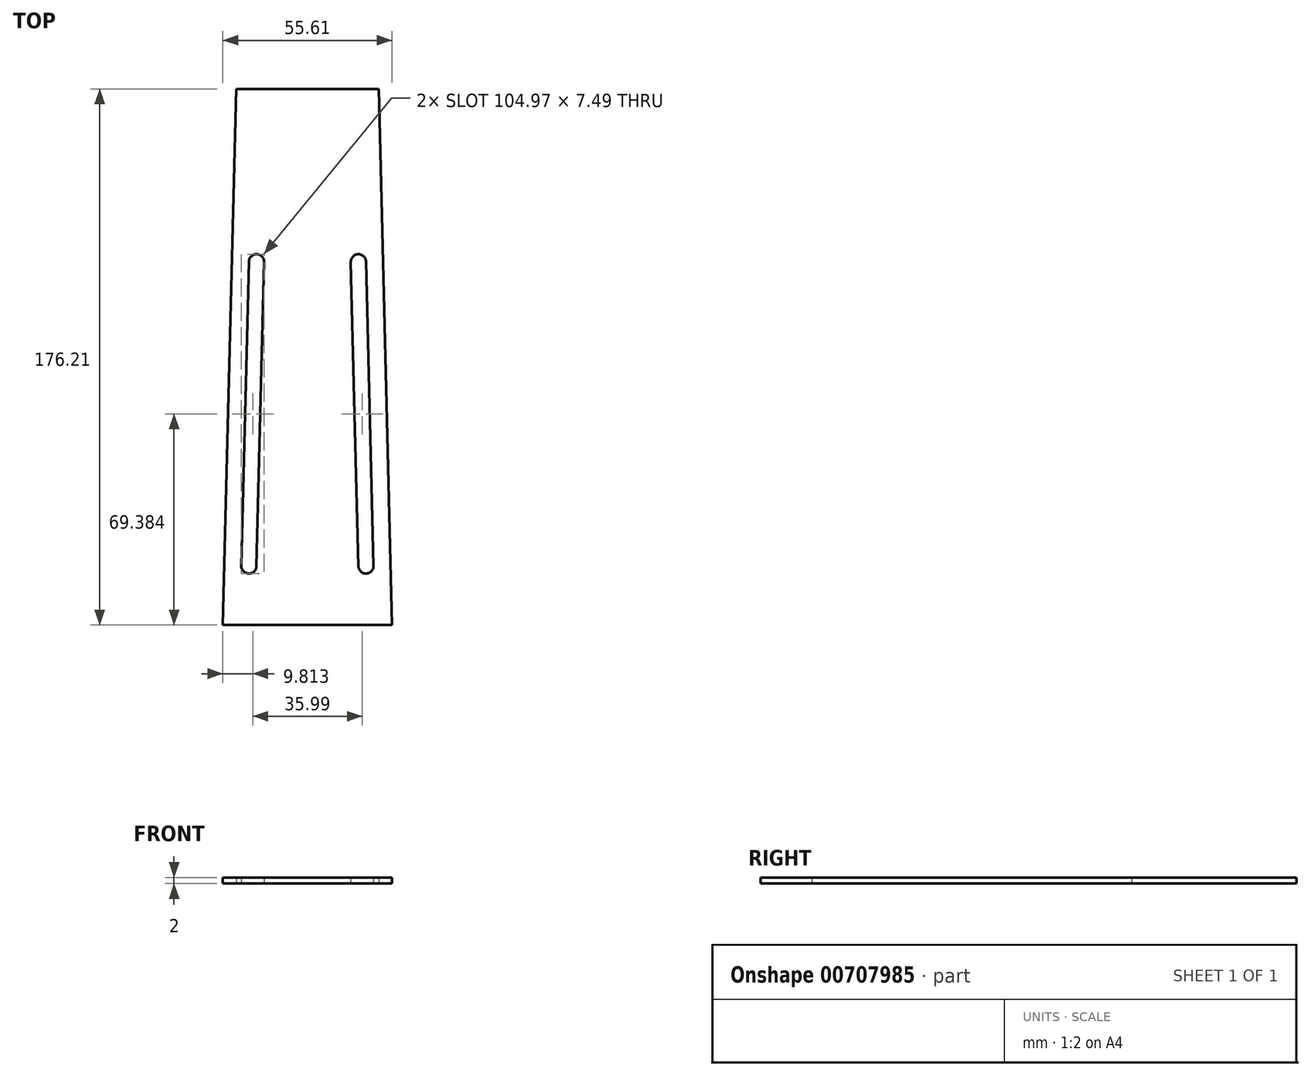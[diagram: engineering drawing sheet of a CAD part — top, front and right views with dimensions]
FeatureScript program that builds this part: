
annotation { "Feature Type Name" : "Feature", "Feature Type Description" : "" }
export const myFeature = defineFeature(function(context is Context, id is Id, definition is map)
    precondition{}
    {
        {
            var Q0;
            Q0=qCreatedBy(makeId("Top.planeOp"), FACE);
            var sketch = newSketch(context, id + "F0", { "sketchPlane" : qUnion([Q0])});
            skLineSegment(sketch, "E0", {"start": v(20.58, -7.45) * mm, "end": v(15.57, -7.45) * mm, "construction": true});
            skLineSegment(sketch, "E1", {"start": v(19.4, 39.84) * mm, "end": v(21.89, -60.13) * mm});
            skLineSegment(sketch, "E2.0", {"start": v(14.4, 39.72) * mm, "end": v(16.9, -60.25) * mm});
            skArc(sketch, "E3", {"start": v(19.4, 39.84) * mm, "mid": v(16.83, 42.28) * mm, "end": v(14.4, 39.72) * mm});
            skArc(sketch, "E4", {"start": v(16.9, -60.25) * mm, "mid": v(19.45, -62.69) * mm, "end": v(21.89, -60.13) * mm});
            skArc(sketch, "E5.MirrorCS", {"start": v(-19.1, 39.84) * mm, "mid": v(-16.54, 42.28) * mm, "end": v(-14.1, 39.72) * mm});
            skArc(sketch, "E6.MirrorCS", {"start": v(-16.6, -60.25) * mm, "mid": v(-19.16, -62.69) * mm, "end": v(-21.6, -60.13) * mm});
            skLineSegment(sketch, "E7.MirrorCS", {"start": v(-14.1, 39.72) * mm, "end": v(-16.6, -60.25) * mm});
            skLineSegment(sketch, "E8.MirrorCS", {"start": v(-19.1, 39.84) * mm, "end": v(-21.6, -60.13) * mm});
            skLineSegment(sketch, "E9.0", {"start": v(23.56, 96.62) * mm, "end": v(27.95, -79.6) * mm});
            skLineSegment(sketch, "E10.0", {"start": v(-23.26, 96.62) * mm, "end": v(-27.66, -79.6) * mm});
            skLineSegment(sketch, "E11", {"start": v(23.56, 96.62) * mm, "end": v(-23.26, 96.62) * mm});
            skLineSegment(sketch, "E12", {"start": v(27.95, -79.6) * mm, "end": v(-27.66, -79.6) * mm});
            skLineSegment(sketch, "E13.trimOffspring", {"start": v(-15.28, -7.45) * mm, "end": v(-20.28, -7.45) * mm, "construction": true});
            skSolve(sketch);
        }
        {
            var Q0;
            Q0 = qSketchRegion(id + "F0", true);
            extrude(context, id + "F1", {"entities" : qUnion([Q0]), "depth" : 2 * mm, "offsetDistance" : 25 * mm});
        }
    });
